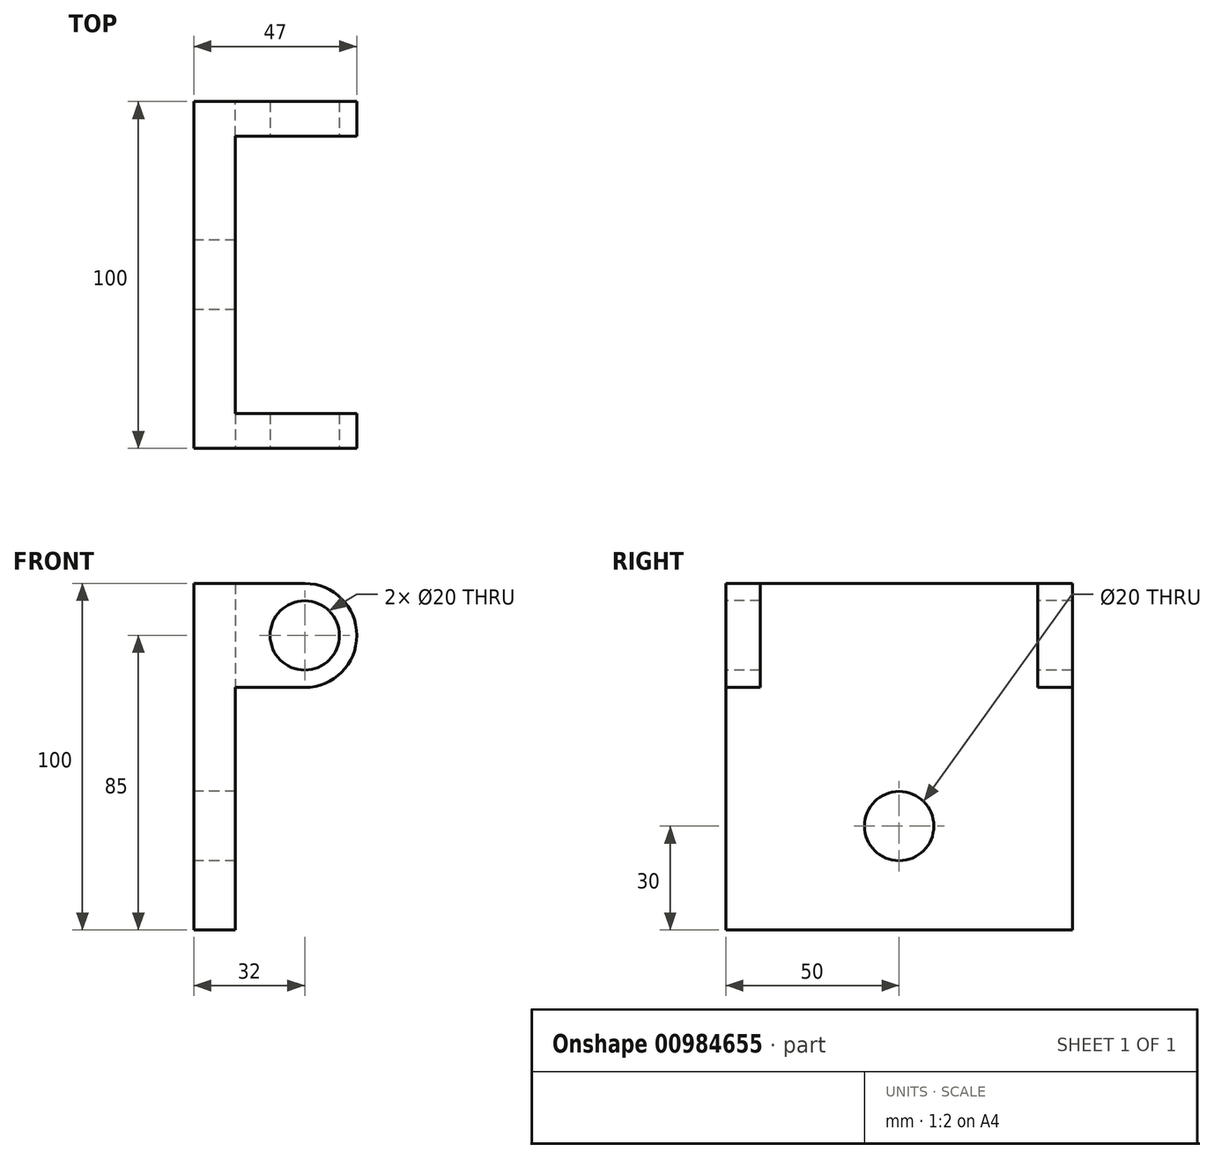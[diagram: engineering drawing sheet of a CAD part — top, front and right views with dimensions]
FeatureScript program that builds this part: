
annotation { "Feature Type Name" : "Feature", "Feature Type Description" : "" }
export const myFeature = defineFeature(function(context is Context, id is Id, definition is map)
    precondition{}
    {
        {
            var Q0;
            Q0=qCreatedBy(makeId("Front.planeOp"),FACE);
            var sketch = newSketch(context, id + "F0", { "sketchPlane" : qUnion([Q0])});
            skLineSegment(sketch, "E0.bottom", {"start": v(0, 0) * mm, "end": v(20, 0) * mm});
            skLineSegment(sketch, "E0.top", {"start": v(0, 30) * mm, "end": v(20, 30) * mm});
            skLineSegment(sketch, "E0.left", {"start": v(0, 0) * mm, "end": v(0, 30) * mm});
            skLineSegment(sketch, "E0.right", {"start": v(20, 0) * mm, "end": v(20, 30) * mm});
            skArc(sketch, "E1", {"start": v(20, 0) * mm, "mid": v(35, 15) * mm, "end": v(20, 30) * mm});
            skCircle(sketch, "E2", {"center": v(20, 15) * mm, "radius": 5 * mm});
            skSolve(sketch);
        }
        {
            var Q0;
            Q0 = qSketchRegion(id + "F0", true);
            extrude(context, id + "F1", {"entities" : qUnion([Q0]), "depth" : 10 * mm, "offsetDistance" : 25 * mm});
        }
        {
            var Q0;
            Q0=qCreatedBy(makeId("Right.planeOp"),FACE);
            var sketch = newSketch(context, id + "F2", { "sketchPlane" : qUnion([Q0])});
            skLineSegment(sketch, "E3.bottom", {"start": v(0, 30) * mm, "end": v(-100, 30) * mm});
            skLineSegment(sketch, "E3.top", {"start": v(0, -70) * mm, "end": v(-100, -70) * mm});
            skLineSegment(sketch, "E3.left", {"start": v(0, 30) * mm, "end": v(0, -70) * mm});
            skLineSegment(sketch, "E3.right", {"start": v(-100, 30) * mm, "end": v(-100, -70) * mm});
            skSolve(sketch);
        }
        {
            var Q0;
            Q0 = qSketchRegion(id + "F2", true);
            extrude(context, id + "F3", {"entities" : qUnion([Q0]), "operationType" : NewBodyOperationType.ADD, "oppositeDirection" : true, "depth" : 12 * mm, "offsetDistance" : 25 * mm});
        }
        {
            var Q0;
            Q0=makeQuery(id+"F3.opExtrude","SWEPT_FACE",FACE,{"disambiguationData":[OSD([sQuery(id+"F2.wireOp",EDGE,"E3.right")])]});
            var sketch = newSketch(context, id + "F4", { "sketchPlane" : qUnion([Q0])});
            skLineSegment(sketch, "E4.bottom", {"start": v(0, 0) * mm, "end": v(20, 0) * mm});
            skLineSegment(sketch, "E4.top", {"start": v(0, 30) * mm, "end": v(20, 30) * mm});
            skLineSegment(sketch, "E4.left", {"start": v(0, 0) * mm, "end": v(0, 30) * mm});
            skLineSegment(sketch, "E4.right", {"start": v(20, 0) * mm, "end": v(20, 30) * mm});
            skArc(sketch, "E5", {"start": v(20, 0) * mm, "mid": v(35, 15) * mm, "end": v(20, 30) * mm});
            skCircle(sketch, "E6", {"center": v(20, 15) * mm, "radius": 5 * mm});
            skSolve(sketch);
        }
        {
            var Q0;
            Q0 = qSketchRegion(id + "F4", true);
            extrude(context, id + "F5", {"entities" : qUnion([Q0]), "operationType" : NewBodyOperationType.ADD, "oppositeDirection" : true, "depth" : 10 * mm, "offsetDistance" : 25 * mm});
        }
        {
            var Q0;
            Q0=makeQuery(id+"F3.opExtrude","CAP_FACE",FACE,{"disambiguationData":[OSD([sQuery(id+"F2.wireOp",EDGE,"E3.bottom"),sQuery(id+"F2.wireOp",EDGE,"E3.top"),sQuery(id+"F2.wireOp",EDGE,"E3.left"),sQuery(id+"F2.wireOp",EDGE,"E3.right")])],"isStart":false});
            var sketch = newSketch(context, id + "F6", { "sketchPlane" : qUnion([Q0])});
            skCircle(sketch, "E7", {"center": v(50, -40) * mm, "radius": 10 * mm});
            skSolve(sketch);
        }
        {
            var Q0;
            Q0=sQuery(id+"F6.wireOp",VERTEX,"E7.center");
            var Q1;
            Q1=makeQuery(id+"F1.opExtrude","SWEPT_BODY",BODY,{"disambiguationData":[OSD([sQuery(id+"F0.wireOp",EDGE,"E0.bottom"),sQuery(id+"F0.wireOp",EDGE,"E0.top"),sQuery(id+"F0.wireOp",EDGE,"E0.left"),sQuery(id+"F0.wireOp",EDGE,"E1"),sQuery(id+"F0.wireOp",EDGE,"E2")])]});
            hole(context, id + "F7", {"style" : HoleStyle.SIMPLE, "endStyle" : HoleEndStyle.THROUGH, "holeDiameter" : 20 * mm, "majorDiameter" : 5 * mm, "isTappedThrough" : true, "tappedDepth" : 12 * mm, "tapClearance" : 3, "locations" : qUnion([Q0]), "scope" : qUnion([Q1])});
        }
        {
            var Q0;
            Q0=makeQuery(id+"F5.boolean.opBoolean","MERGE",FACE,{"derivedFrom":[makeQuery(id+"F3.opExtrude","SWEPT_FACE",FACE,{"disambiguationData":[OSD([sQuery(id+"F2.wireOp",EDGE,"E3.right")])]}),makeQuery(id+"F5.opExtrude","CAP_FACE",FACE,{"disambiguationData":[OSD([sQuery(id+"F4.wireOp",EDGE,"E4.bottom"),sQuery(id+"F4.wireOp",EDGE,"E4.top"),sQuery(id+"F4.wireOp",EDGE,"E4.left"),sQuery(id+"F4.wireOp",EDGE,"E5"),sQuery(id+"F4.wireOp",EDGE,"E6")])],"isStart":true})]});
            var sketch = newSketch(context, id + "F8", { "sketchPlane" : qUnion([Q0])});
            skPoint(sketch, "E8", {"position": v(20, 15) * mm});
            skSolve(sketch);
        }
        {
            var Q0;
            Q0=sQuery(id+"F8.wireOp",VERTEX,"E8");
            var Q1;
            Q1=makeQuery(id+"F1.opExtrude","SWEPT_BODY",BODY,{"disambiguationData":[OSD([sQuery(id+"F0.wireOp",EDGE,"E0.bottom"),sQuery(id+"F0.wireOp",EDGE,"E0.top"),sQuery(id+"F0.wireOp",EDGE,"E0.left"),sQuery(id+"F0.wireOp",EDGE,"E1"),sQuery(id+"F0.wireOp",EDGE,"E2")])]});
            hole(context, id + "F9", {"style" : HoleStyle.SIMPLE, "endStyle" : HoleEndStyle.THROUGH, "holeDiameter" : 20 * mm, "majorDiameter" : 5 * mm, "isTappedThrough" : true, "tappedDepth" : 12 * mm, "tapClearance" : 3, "locations" : qUnion([Q0]), "scope" : qUnion([Q1])});
        }
    });
